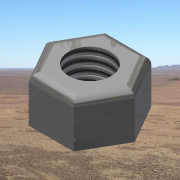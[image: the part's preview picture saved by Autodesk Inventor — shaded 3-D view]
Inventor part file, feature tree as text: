
AUTODESK INVENTOR PART (.ipt)
format: ipt  version: 2013 SP2 (Build 170200200, 200)  size: 145,408 bytes
history: native  units: in
note: dims shown in document units (in); Inventor stores cm internally (conversion verified against a paired STEP export)
features: sketch x2, extrude x1, hole x1, fillet x1
ambient origin geometry x8: Origin, YZ Plane, XZ Plane, XY Plane, X Axis, Y Axis, Z Axis, Center Point
bodies: Solid1 (feature_tree)
feature tree (5):
  extrude  "Extrusion1"  Depth=0.3281in TaperAngle=0.0deg
  hole  "Hole1"  [1 undecoded]
  fillet  "Fillet1"  [1 undecoded]
  sketch  "Sketch1"  dims[d0=0.5625in d1=0.3281in d2=0.0in]
  sketch  "Sketch2"  dims[d3=0.375in d5=0.307in d6=0.75in d7=0.375in d8=0.25in d9=0.5635in d10=1.0in d11=0.8108in d12=0.06in]
note: 2 required parameter values undecoded (feature->parameter linkage not recoverable at this tier; creation-order binding heuristic only, values carry confidence <= 0.55)
